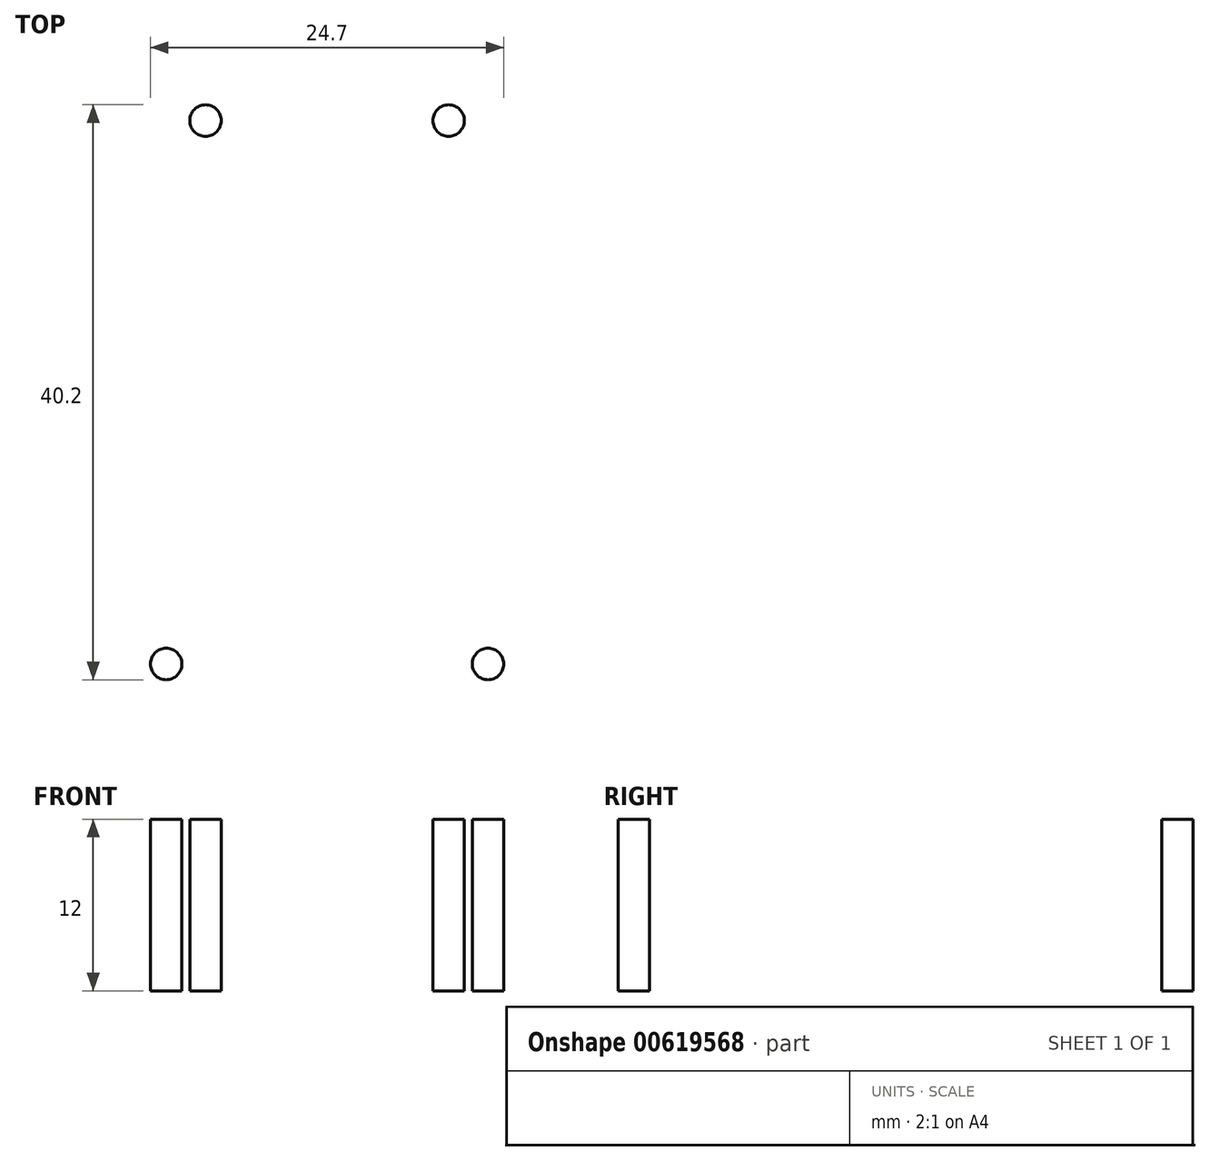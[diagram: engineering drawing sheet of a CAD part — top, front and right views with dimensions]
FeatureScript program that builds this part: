
annotation { "Feature Type Name" : "Feature", "Feature Type Description" : "" }
export const myFeature = defineFeature(function(context is Context, id is Id, definition is map)
    precondition{}
    {
        {
            var Q0;
            Q0=qCreatedBy(makeId("Top.planeOp"),FACE);
            var sketch = newSketch(context, id + "F0", { "sketchPlane" : qUnion([Q0])});
            skCircle(sketch, "E0", {"center": v(-8.5, 19) * mm, "radius": 1.1 * mm});
            skCircle(sketch, "E1", {"center": v(-11.25, -19) * mm, "radius": 1.1 * mm});
            skCircle(sketch, "E2.MirrorC", {"center": v(11.25, -19) * mm, "radius": 1.1 * mm});
            skCircle(sketch, "E3.MirrorC", {"center": v(8.5, 19) * mm, "radius": 1.1 * mm});
            skSolve(sketch);
        }
        {
            var Q0;
            Q0 = qSketchRegion(id + "F0", true);
            extrude(context, id + "F1", {"entities" : qUnion([Q0]), "depth" : 12 * mm, "offsetDistance" : 25 * mm});
        }
    });
